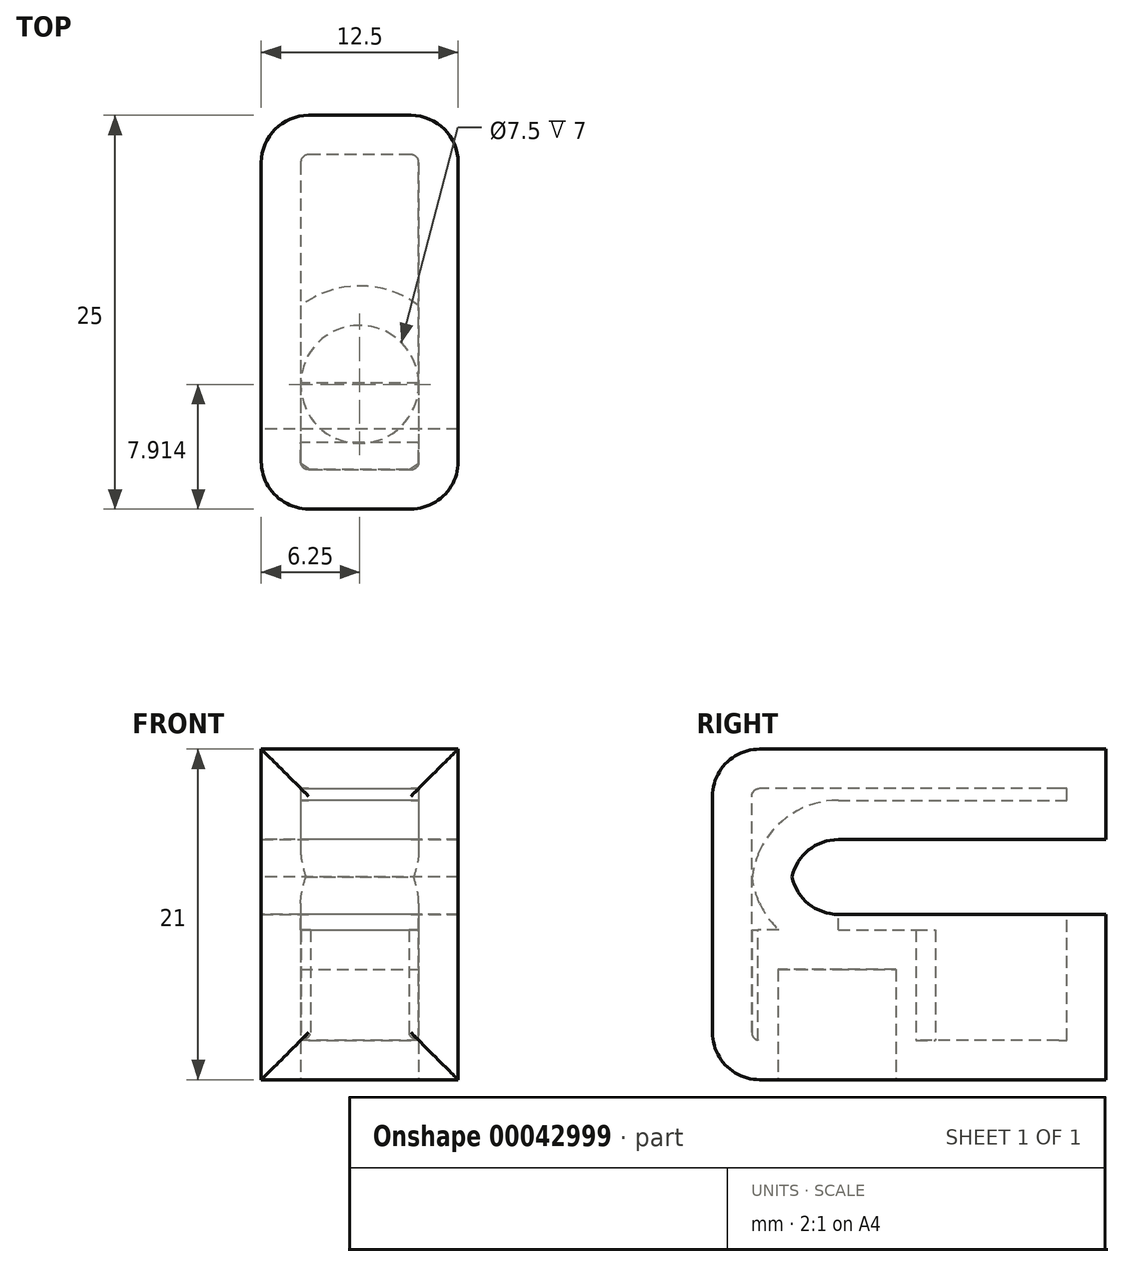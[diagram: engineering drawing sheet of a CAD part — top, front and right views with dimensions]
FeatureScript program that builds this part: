
annotation { "Feature Type Name" : "Feature", "Feature Type Description" : "" }
export const myFeature = defineFeature(function(context is Context, id is Id, definition is map)
    precondition{}
    {
        {
            var Q0;
            Q0=qCreatedBy(makeId("Top.planeOp"),FACE);
            var sketch = newSketch(context, id + "F0", { "sketchPlane" : qUnion([Q0])});
            skLineSegment(sketch, "E0.bottom", {"start": v(-12.5, 0) * mm, "end": v(0, 0) * mm});
            skLineSegment(sketch, "E0.top", {"start": v(-12.5, -25) * mm, "end": v(0, -25) * mm});
            skLineSegment(sketch, "E0.left", {"start": v(-12.5, 0) * mm, "end": v(-12.5, -25) * mm});
            skLineSegment(sketch, "E0.right", {"start": v(0, 0) * mm, "end": v(0, -25) * mm});
            skSolve(sketch);
        }
        {
            var Q0;
            Q0=makeQuery(id+"F0.imprint","IMPRINT",FACE,{"disambiguationData":[TD([[makeQuery(id+"F0.imprint","IMPRINT",EDGE,{"derivedFrom":sQuery(id+"F0.wireOp",EDGE,"E0.bottom")}),-1.0]])]});
            extrude(context, id + "F1", {"entities" : qUnion([Q0]), "depth" : 21 * mm});
        }
        {
            var Q0;
            Q0=makeQuery(id+"F1.opExtrude","SWEPT_FACE",FACE,{"disambiguationData":[OSD([sQuery(id+"F0.wireOp",EDGE,"E0.left")])]});
            var sketch = newSketch(context, id + "F2", { "sketchPlane" : qUnion([Q0])});
            skLineSegment(sketch, "E1.bottom", {"start": v(0, 15.25) * mm, "end": v(20, 15.25) * mm});
            skLineSegment(sketch, "E1.top", {"start": v(0, 10.5) * mm, "end": v(20, 10.5) * mm});
            skLineSegment(sketch, "E1.left", {"start": v(0, 15.25) * mm, "end": v(0, 10.5) * mm});
            skLineSegment(sketch, "E1.right", {"start": v(20, 15.25) * mm, "end": v(20, 10.5) * mm});
            skSolve(sketch);
        }
        {
            var Q0;
            Q0=makeQuery(id+"F2.imprint","IMPRINT",FACE,{"disambiguationData":[TD([[makeQuery(id+"F2.imprint","IMPRINT",EDGE,{"derivedFrom":sQuery(id+"F2.wireOp",EDGE,"E1.bottom")}),-1.0]])]});
            extrude(context, id + "F3", {"entities" : qUnion([Q0]), "operationType" : NewBodyOperationType.REMOVE, "oppositeDirection" : true, "depth" : 25 * mm});
        }
        {
            var Q0;
            Q0=qCreatedBy(makeId("Top.planeOp"),FACE);
            var sketch = newSketch(context, id + "F4", { "sketchPlane" : qUnion([Q0])});
            skPoint(sketch, "E2", {"position": v(0, 0) * mm});
            skPoint(sketch, "E3", {"position": v(-12.14, 0) * mm});
            skPoint(sketch, "E4", {"position": v(-6.07, 0) * mm});
            skLineSegment(sketch, "E5", {"start": v(-6.07, 0) * mm, "end": v(-6.07, -23.52) * mm});
            skCircle(sketch, "E6", {"center": v(-6.07, -7) * mm, "radius": 3.75 * mm});
            skSolve(sketch);
        }
        {
            var Q0;
            {var subQ0=sQuery(id+"F4.wireOp",EDGE,"E6");var subQ1=sQuery(id+"F4.wireOp",EDGE,"E5");var subQ3=makeQuery(id+"F4.imprint","INTERSECT",VERTEX,{"disambiguationData":[OD(0.0)],"derivedFrom":[subQ1,subQ0]});Q0=makeQuery(id+"F4.imprint","IMPRINT",FACE,{"disambiguationData":[TD([[makeQuery(id+"F4.imprint","IMPRINT",EDGE,{"disambiguationData":[TD([[subQ3,1.0]])],"derivedFrom":subQ1}),1.0]])]});}
            var Q1;
            {var subQ0=sQuery(id+"F4.wireOp",EDGE,"E6");var subQ1=sQuery(id+"F4.wireOp",EDGE,"E5");var subQ3=makeQuery(id+"F4.imprint","INTERSECT",VERTEX,{"disambiguationData":[OD(0.0)],"derivedFrom":[subQ1,subQ0]});Q1=makeQuery(id+"F4.imprint","IMPRINT",FACE,{"disambiguationData":[TD([[makeQuery(id+"F4.imprint","IMPRINT",EDGE,{"disambiguationData":[TD([[subQ3,1.0]])],"derivedFrom":subQ1}),-1.0]])]});}
            extrude(context, id + "F5", {"entities" : qUnion([Q0, Q1]), "operationType" : NewBodyOperationType.REMOVE, "oppositeDirection" : true, "depth" : 25 * mm});
        }
        {
            var Q0;
            Q0=makeQuery(id+"F1.opExtrude","CAP_FACE",FACE,{"disambiguationData":[OSD([sQuery(id+"F0.wireOp",EDGE,"E0.bottom"),sQuery(id+"F0.wireOp",EDGE,"E0.top"),sQuery(id+"F0.wireOp",EDGE,"E0.left"),sQuery(id+"F0.wireOp",EDGE,"E0.right")])],"isStart":true});
            var sketch = newSketch(context, id + "F6", { "sketchPlane" : qUnion([Q0])});
            skPoint(sketch, "E7", {"position": v(-12.5, 0) * mm});
            skPoint(sketch, "E8", {"position": v(-6.25, 0) * mm});
            skPoint(sketch, "E9", {"position": v(0, 0) * mm});
            skLineSegment(sketch, "E10", {"start": v(-6.25, 0) * mm, "end": v(-6.25, 25) * mm});
            skCircle(sketch, "E11", {"center": v(-6.25, 17.09) * mm, "radius": 3.75 * mm});
            skSolve(sketch);
        }
        {
            var Q0;
            {var subQ0=sQuery(id+"F6.wireOp",EDGE,"E11");var subQ1=sQuery(id+"F6.wireOp",EDGE,"E10");var subQ3=makeQuery(id+"F6.imprint","INTERSECT",VERTEX,{"disambiguationData":[OD(0.0)],"derivedFrom":[subQ1,subQ0]});Q0=makeQuery(id+"F6.imprint","IMPRINT",FACE,{"disambiguationData":[TD([[makeQuery(id+"F6.imprint","IMPRINT",EDGE,{"disambiguationData":[TD([[subQ3,-1.0]])],"derivedFrom":subQ1}),-1.0]])]});}
            var Q1;
            {var subQ0=sQuery(id+"F6.wireOp",EDGE,"E11");var subQ1=sQuery(id+"F6.wireOp",EDGE,"E10");var subQ3=makeQuery(id+"F6.imprint","INTERSECT",VERTEX,{"disambiguationData":[OD(0.0)],"derivedFrom":[subQ1,subQ0]});Q1=makeQuery(id+"F6.imprint","IMPRINT",FACE,{"disambiguationData":[TD([[makeQuery(id+"F6.imprint","IMPRINT",EDGE,{"disambiguationData":[TD([[subQ3,-1.0]])],"derivedFrom":subQ1}),1.0]])]});}
            extrude(context, id + "F7", {"entities" : qUnion([Q0, Q1]), "operationType" : NewBodyOperationType.REMOVE, "oppositeDirection" : true, "depth" : 7 * mm});
        }
        {
            var Q0;
            {var subQ0=sQuery(id+"F0.wireOp",EDGE,"E0.bottom");var subQ1=sQuery(id+"F0.wireOp",EDGE,"E0.left");Q0=makeQuery(id+"F3.boolean.opBoolean","SPLIT",EDGE,{"disambiguationData":[TD([makeQuery(id+"F3.opExtrude","SWEPT_FACE",FACE,{"disambiguationData":[OSD([sQuery(id+"F2.wireOp",EDGE,"E1.bottom")])]})])],"derivedFrom":makeQuery(id+"F1.opExtrude","SWEPT_EDGE",EDGE,{"disambiguationData":[OSD([subQ0,subQ1])]})});}
            var Q1;
            {var subQ0=sQuery(id+"F0.wireOp",EDGE,"E0.bottom");var subQ1=sQuery(id+"F0.wireOp",EDGE,"E0.right");Q1=makeQuery(id+"F3.boolean.opBoolean","SPLIT",EDGE,{"disambiguationData":[TD([makeQuery(id+"F3.opExtrude","SWEPT_FACE",FACE,{"disambiguationData":[OSD([sQuery(id+"F2.wireOp",EDGE,"E1.bottom")])]})])],"derivedFrom":makeQuery(id+"F1.opExtrude","SWEPT_EDGE",EDGE,{"disambiguationData":[OSD([subQ0,subQ1])]})});}
            var Q2;
            {var subQ0=sQuery(id+"F0.wireOp",EDGE,"E0.bottom");var subQ1=sQuery(id+"F0.wireOp",EDGE,"E0.left");Q2=makeQuery(id+"F3.boolean.opBoolean","SPLIT",EDGE,{"disambiguationData":[TD([makeQuery(id+"F3.opExtrude","SWEPT_FACE",FACE,{"disambiguationData":[OSD([sQuery(id+"F2.wireOp",EDGE,"E1.top")])]})])],"derivedFrom":makeQuery(id+"F1.opExtrude","SWEPT_EDGE",EDGE,{"disambiguationData":[OSD([subQ0,subQ1])]})});}
            var Q3;
            {var subQ0=sQuery(id+"F0.wireOp",EDGE,"E0.bottom");var subQ1=sQuery(id+"F0.wireOp",EDGE,"E0.right");Q3=makeQuery(id+"F3.boolean.opBoolean","SPLIT",EDGE,{"disambiguationData":[TD([makeQuery(id+"F3.opExtrude","SWEPT_FACE",FACE,{"disambiguationData":[OSD([sQuery(id+"F2.wireOp",EDGE,"E1.top")])]})])],"derivedFrom":makeQuery(id+"F1.opExtrude","SWEPT_EDGE",EDGE,{"disambiguationData":[OSD([subQ0,subQ1])]})});}
            var Q4;
            Q4=makeQuery(id+"F1.opExtrude","SWEPT_EDGE",EDGE,{"disambiguationData":[OSD([sQuery(id+"F0.wireOp",EDGE,"E0.top"),sQuery(id+"F0.wireOp",EDGE,"E0.left")])]});
            var Q5;
            Q5=makeQuery(id+"F1.opExtrude","SWEPT_EDGE",EDGE,{"disambiguationData":[OSD([sQuery(id+"F0.wireOp",EDGE,"E0.top"),sQuery(id+"F0.wireOp",EDGE,"E0.right")])]});
            var Q6;
            Q6=makeQuery(id+"F1.opExtrude","CAP_EDGE",EDGE,{"disambiguationData":[OSD([sQuery(id+"F0.wireOp",EDGE,"E0.top")])],"isStart":true});
            var Q7;
            Q7=makeQuery(id+"F1.opExtrude","CAP_EDGE",EDGE,{"disambiguationData":[OSD([sQuery(id+"F0.wireOp",EDGE,"E0.top")])],"isStart":false});
            var Q8;
            Q8=makeQuery(id+"F3.boolean.opBoolean","COPY",EDGE,{"derivedFrom":makeQuery(id+"F3.opExtrude","SWEPT_EDGE",EDGE,{"disambiguationData":[OSD([sQuery(id+"F2.wireOp",EDGE,"E1.top"),sQuery(id+"F2.wireOp",EDGE,"E1.right")])]})});
            var Q9;
            Q9=makeQuery(id+"F3.boolean.opBoolean","COPY",EDGE,{"derivedFrom":makeQuery(id+"F3.opExtrude","SWEPT_EDGE",EDGE,{"disambiguationData":[OSD([sQuery(id+"F2.wireOp",EDGE,"E1.bottom"),sQuery(id+"F2.wireOp",EDGE,"E1.right")])]})});
            fillet(context, id + "F8", {"entities" : qUnion([Q0, Q1, Q2, Q3, Q4, Q5, Q6, Q7, Q8, Q9]), "radius" : 3 * mm, "tangentPropagation" : true, "allowEdgeOverflow" : false});
        }
        {
            var Q0;
            Q0=makeQuery(id+"F3.boolean.opBoolean","COPY",FACE,{"derivedFrom":makeQuery(id+"F3.opExtrude","SWEPT_FACE",FACE,{"disambiguationData":[OSD([sQuery(id+"F2.wireOp",EDGE,"E1.top")])]})});
            shell(context, id + "F9", {"entities" : qUnion([Q0]), "thickness" : 2.5 * mm});
        }
    });
